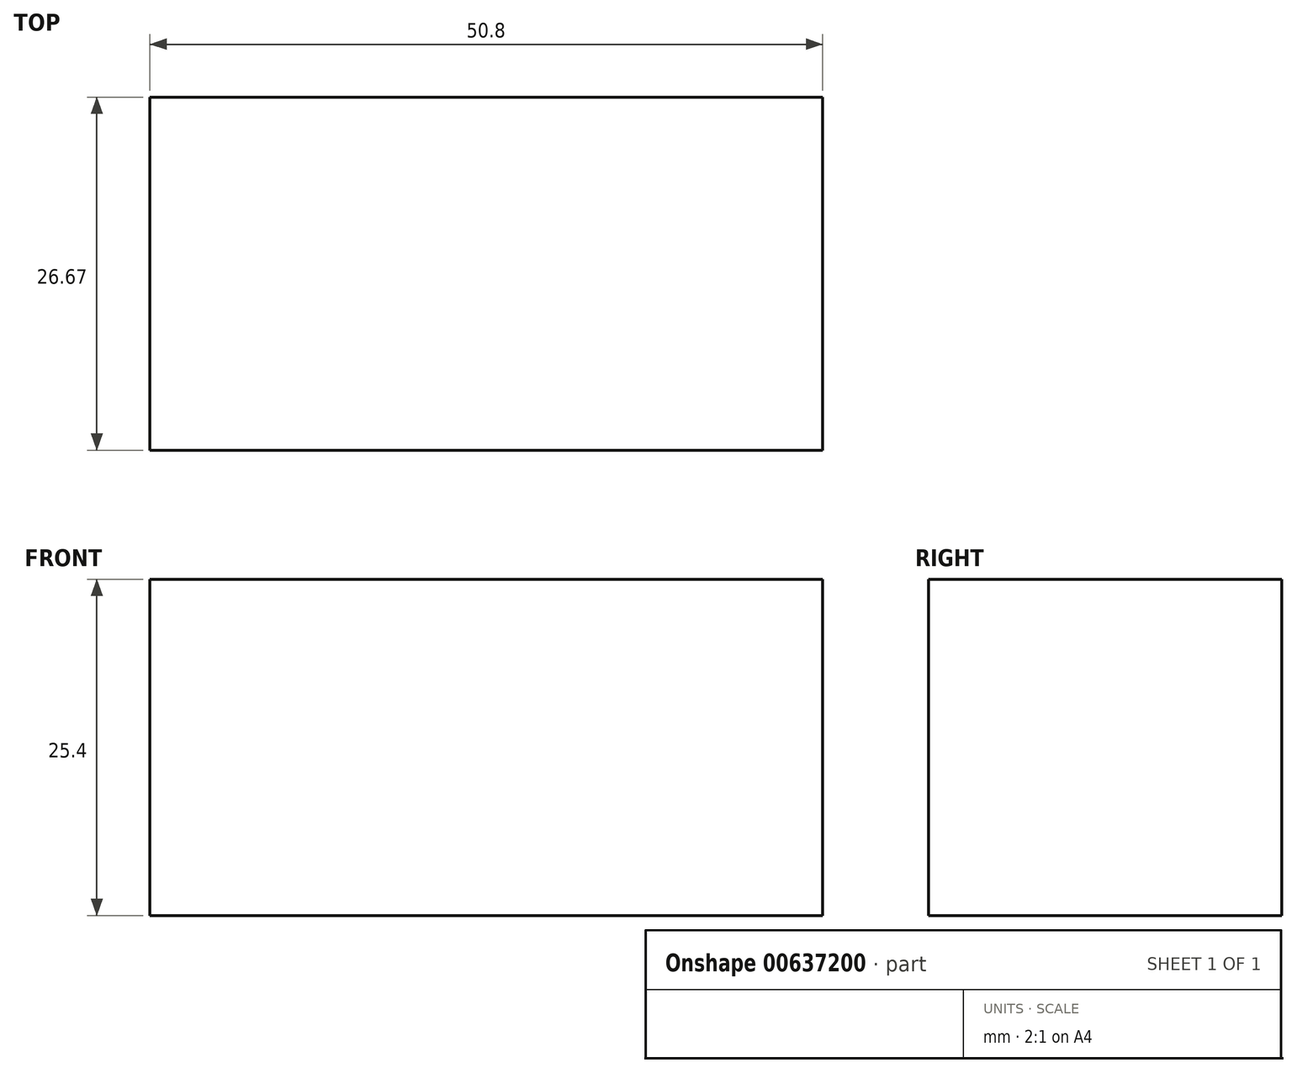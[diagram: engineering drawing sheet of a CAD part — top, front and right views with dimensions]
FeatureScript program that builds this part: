
annotation { "Feature Type Name" : "Feature", "Feature Type Description" : "" }
export const myFeature = defineFeature(function(context is Context, id is Id, definition is map)
    precondition{}
    {
        {
            var Q0;
            Q0=qCreatedBy(makeId("Top.planeOp"),FACE);
            var sketch = newSketch(context, id + "F0", { "sketchPlane" : qUnion([Q0])});
            skLineSegment(sketch, "E0", {"start": v(-40.83, 19.28) * mm, "end": v(9.97, 19.28) * mm});
            skLineSegment(sketch, "E1", {"start": v(9.97, 19.28) * mm, "end": v(9.97, -7.4) * mm});
            skLineSegment(sketch, "E2", {"start": v(9.97, -7.4) * mm, "end": v(-40.83, -7.4) * mm});
            skLineSegment(sketch, "E3", {"start": v(-40.83, -7.4) * mm, "end": v(-40.83, 19.28) * mm});
            skSolve(sketch);
        }
        {
            var Q0;
            Q0 = qSketchRegion(id + "F0", true);
            extrude(context, id + "F1", {"entities" : qUnion([Q0]), "depth" : 25.4 * mm, "offsetDistance" : 25.4 * mm});
        }
    });
